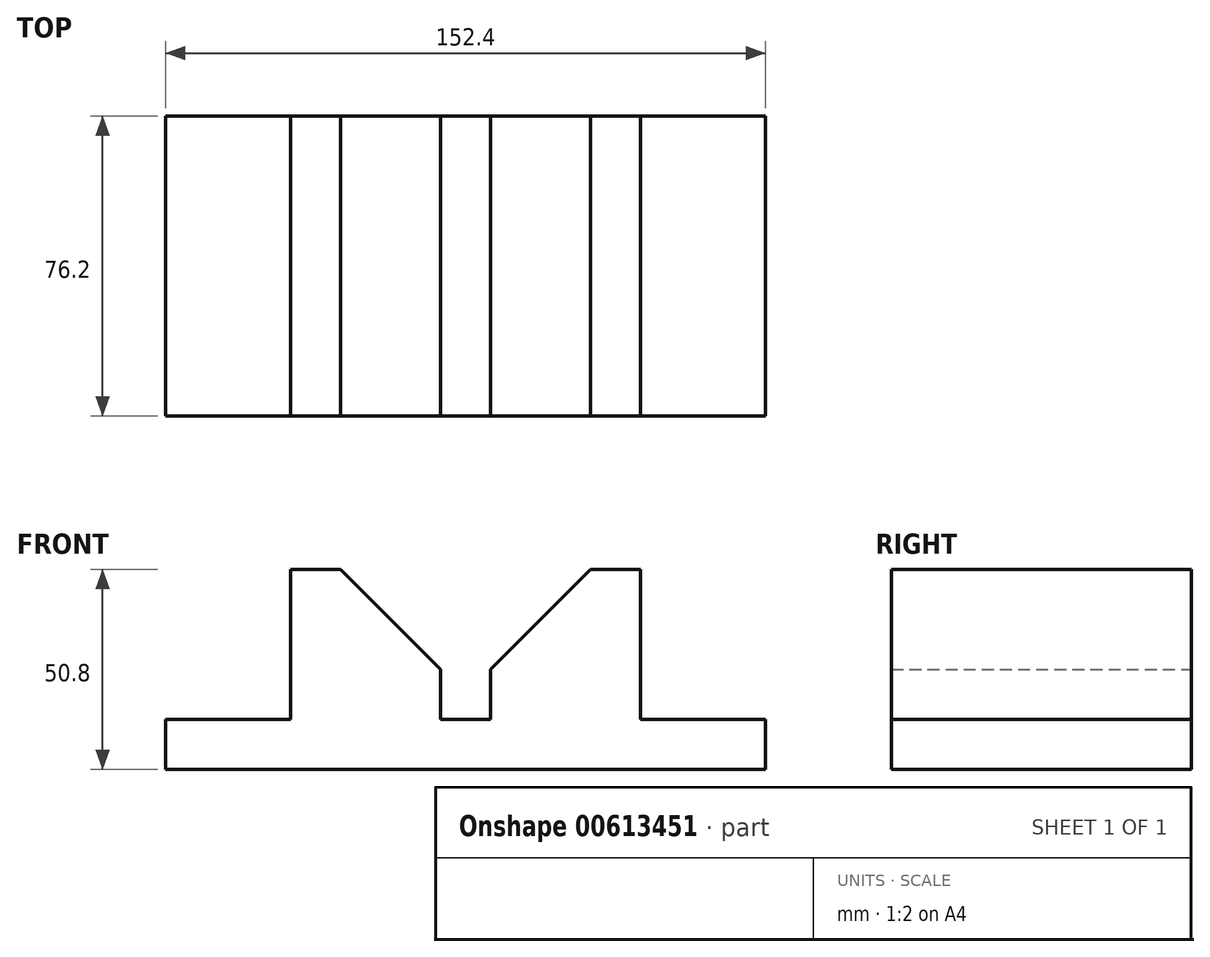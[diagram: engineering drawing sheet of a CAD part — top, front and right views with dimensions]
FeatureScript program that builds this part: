
annotation { "Feature Type Name" : "Feature", "Feature Type Description" : "" }
export const myFeature = defineFeature(function(context is Context, id is Id, definition is map)
    precondition{}
    {
        {
            var Q0;
            Q0=qCreatedBy(makeId("Front.planeOp"),FACE);
            var sketch = newSketch(context, id + "F0", { "sketchPlane" : qUnion([Q0])});
            skLineSegment(sketch, "E0", {"start": v(0, 0) * mm, "end": v(0, 12.7) * mm});
            skLineSegment(sketch, "E1", {"start": v(0, 12.7) * mm, "end": v(31.75, 12.7) * mm});
            skLineSegment(sketch, "E2", {"start": v(31.75, 12.7) * mm, "end": v(31.75, 50.8) * mm});
            skLineSegment(sketch, "E3", {"start": v(31.75, 50.8) * mm, "end": v(44.45, 50.8) * mm});
            skLineSegment(sketch, "E4", {"start": v(0, 0) * mm, "end": v(152.4, 0) * mm});
            skLineSegment(sketch, "E5", {"start": v(152.4, 0) * mm, "end": v(152.4, 12.7) * mm});
            skLineSegment(sketch, "E6", {"start": v(152.4, 12.7) * mm, "end": v(120.65, 12.7) * mm});
            skLineSegment(sketch, "E7", {"start": v(120.65, 12.7) * mm, "end": v(120.65, 50.8) * mm});
            skLineSegment(sketch, "E8", {"start": v(120.65, 50.8) * mm, "end": v(107.95, 50.8) * mm});
            skLineSegment(sketch, "E9", {"start": v(76.2, 12.7) * mm, "end": v(69.85, 12.7) * mm});
            skLineSegment(sketch, "E10", {"start": v(76.2, 12.7) * mm, "end": v(82.55, 12.7) * mm});
            skLineSegment(sketch, "E11", {"start": v(82.55, 12.7) * mm, "end": v(82.55, 25.4) * mm});
            skLineSegment(sketch, "E12", {"start": v(69.85, 12.7) * mm, "end": v(69.85, 25.4) * mm});
            skLineSegment(sketch, "E13", {"start": v(69.85, 25.4) * mm, "end": v(44.45, 50.8) * mm});
            skLineSegment(sketch, "E14", {"start": v(82.55, 25.4) * mm, "end": v(107.95, 50.8) * mm});
            skSolve(sketch);
        }
        {
            var Q0;
            Q0 = qSketchRegion(id + "F0", true);
            extrude(context, id + "F1", {"entities" : qUnion([Q0]), "depth" : 76.2 * mm, "offsetDistance" : 25.4 * mm});
        }
    });
